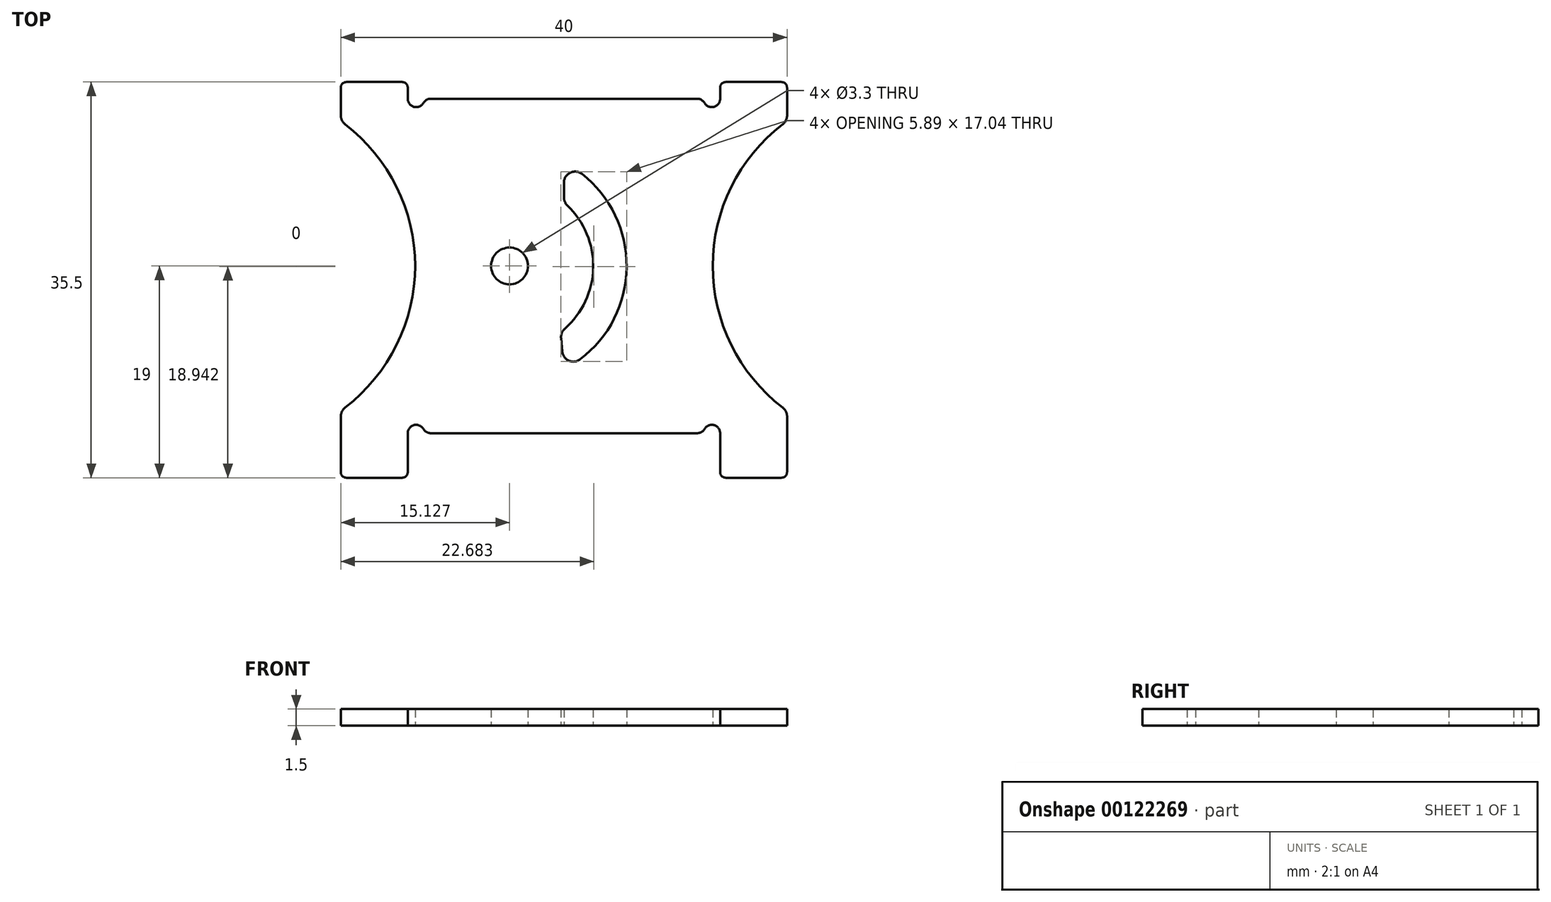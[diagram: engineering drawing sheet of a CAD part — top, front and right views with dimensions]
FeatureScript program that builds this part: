
annotation { "Feature Type Name" : "Feature", "Feature Type Description" : "" }
export const myFeature = defineFeature(function(context is Context, id is Id, definition is map)
    precondition{}
    {
        {
            var Q0;
            Q0=qCreatedBy(makeId("Top.planeOp"),FACE);
            var sketch = newSketch(context, id + "F0", { "sketchPlane" : qUnion([Q0])});
            skArc(sketch, "E0", {"start": v(19.6, 13.95) * mm, "mid": v(19.9, 14.3) * mm, "end": v(20, 14.74) * mm});
            skLineSegment(sketch, "E1", {"start": v(20, 14.74) * mm, "end": v(20, 17.25) * mm});
            skArc(sketch, "E2", {"start": v(20, 17.25) * mm, "mid": v(19.85, 17.6) * mm, "end": v(19.5, 17.75) * mm});
            skLineSegment(sketch, "E3", {"start": v(19.5, 17.75) * mm, "end": v(14.5, 17.75) * mm});
            skArc(sketch, "E4", {"start": v(14.5, 17.75) * mm, "mid": v(14.15, 17.6) * mm, "end": v(14, 17.25) * mm});
            skLineSegment(sketch, "E5", {"start": v(14, 17.25) * mm, "end": v(14, 16.25) * mm});
            skArc(sketch, "E6", {"start": v(12.6, 15.87) * mm, "mid": v(13.44, 15.53) * mm, "end": v(14, 16.25) * mm});
            skArc(sketch, "E7", {"start": v(12.6, 15.88) * mm, "mid": v(12.33, 16.15) * mm, "end": v(11.95, 16.25) * mm});
            skLineSegment(sketch, "E8", {"start": v(11.95, 16.25) * mm, "end": v(-11.95, 16.25) * mm});
            skArc(sketch, "E9", {"start": v(-11.95, 16.25) * mm, "mid": v(-12.33, 16.15) * mm, "end": v(-12.6, 15.88) * mm});
            skArc(sketch, "E10", {"start": v(-14, 16.25) * mm, "mid": v(-13.44, 15.53) * mm, "end": v(-12.6, 15.87) * mm});
            skLineSegment(sketch, "E11", {"start": v(-14, 16.25) * mm, "end": v(-14, 17.25) * mm});
            skArc(sketch, "E12", {"start": v(-14, 17.25) * mm, "mid": v(-14.15, 17.6) * mm, "end": v(-14.5, 17.75) * mm});
            skLineSegment(sketch, "E13", {"start": v(-14.5, 17.75) * mm, "end": v(-19.5, 17.75) * mm});
            skArc(sketch, "E14", {"start": v(-19.5, 17.75) * mm, "mid": v(-19.85, 17.6) * mm, "end": v(-20, 17.25) * mm});
            skLineSegment(sketch, "E15", {"start": v(-20, 17.25) * mm, "end": v(-20, 14.74) * mm});
            skArc(sketch, "E16", {"start": v(-20, 14.74) * mm, "mid": v(-19.9, 14.3) * mm, "end": v(-19.6, 13.95) * mm});
            skArc(sketch, "E17", {"start": v(-19.6, -11.45) * mm, "mid": v(-13.34, 1.25) * mm, "end": v(-19.6, 13.95) * mm});
            skArc(sketch, "E18", {"start": v(-19.6, -11.45) * mm, "mid": v(-19.9, -11.8) * mm, "end": v(-20, -12.24) * mm});
            skLineSegment(sketch, "E19", {"start": v(-20, -12.24) * mm, "end": v(-20, -17.25) * mm});
            skArc(sketch, "E20", {"start": v(-20, -17.25) * mm, "mid": v(-19.85, -17.6) * mm, "end": v(-19.5, -17.75) * mm});
            skLineSegment(sketch, "E21", {"start": v(-19.5, -17.75) * mm, "end": v(-14.5, -17.75) * mm});
            skArc(sketch, "E22", {"start": v(-14.5, -17.75) * mm, "mid": v(-14.15, -17.6) * mm, "end": v(-14, -17.25) * mm});
            skLineSegment(sketch, "E23", {"start": v(-14, -17.25) * mm, "end": v(-14, -13.75) * mm});
            skArc(sketch, "E24", {"start": v(-12.6, -13.37) * mm, "mid": v(-13.44, -13.03) * mm, "end": v(-14, -13.75) * mm});
            skArc(sketch, "E25", {"start": v(-12.6, -13.38) * mm, "mid": v(-12.33, -13.65) * mm, "end": v(-11.95, -13.75) * mm});
            skLineSegment(sketch, "E26", {"start": v(-11.95, -13.75) * mm, "end": v(11.95, -13.75) * mm});
            skArc(sketch, "E27", {"start": v(11.95, -13.75) * mm, "mid": v(12.33, -13.65) * mm, "end": v(12.6, -13.38) * mm});
            skArc(sketch, "E28", {"start": v(14, -13.75) * mm, "mid": v(13.44, -13.03) * mm, "end": v(12.6, -13.37) * mm});
            skLineSegment(sketch, "E29", {"start": v(14, -13.75) * mm, "end": v(14, -17.25) * mm});
            skArc(sketch, "E30", {"start": v(14, -17.25) * mm, "mid": v(14.15, -17.6) * mm, "end": v(14.5, -17.75) * mm});
            skLineSegment(sketch, "E31", {"start": v(14.5, -17.75) * mm, "end": v(19.5, -17.75) * mm});
            skArc(sketch, "E32", {"start": v(19.5, -17.75) * mm, "mid": v(19.85, -17.6) * mm, "end": v(20, -17.25) * mm});
            skLineSegment(sketch, "E33", {"start": v(20, -17.25) * mm, "end": v(20, -12.24) * mm});
            skArc(sketch, "E34", {"start": v(20, -12.24) * mm, "mid": v(19.9, -11.8) * mm, "end": v(19.6, -11.45) * mm});
            skArc(sketch, "E35", {"start": v(19.6, 13.95) * mm, "mid": v(13.34, 1.25) * mm, "end": v(19.6, -11.45) * mm});
            skLineSegment(sketch, "E36", {"start": v(2.63, 1.25) * mm, "end": v(-4.87, 1.25) * mm, "construction": true});
            skCircle(sketch, "E37", {"center": v(-4.87, 1.25) * mm, "radius": 1.65 * mm});
            skArc(sketch, "E38", {"start": v(2.63, 1.25) * mm, "mid": v(1.94, 4.39) * mm, "end": v(0, 6.95) * mm});
            skArc(sketch, "E39.MirrorCS", {"start": v(2.63, 1.25) * mm, "mid": v(1.85, -2.07) * mm, "end": v(-0.3, -4.7) * mm});
            skArc(sketch, "E40", {"start": v(5.63, 1.25) * mm, "mid": v(4.11, -4.19) * mm, "end": v(0, -8.05) * mm});
            skArc(sketch, "E41.MirrorCS", {"start": v(5.63, 1.25) * mm, "mid": v(4.11, 6.69) * mm, "end": v(0, 10.55) * mm});
            skLineSegment(sketch, "E42", {"start": v(0, 10.55) * mm, "end": v(0, 6.95) * mm});
            skLineSegment(sketch, "E43", {"start": v(0, -8.05) * mm, "end": v(-0.3, -4.7) * mm});
            skSolve(sketch);
        }
        {
            var Q0;
            Q0=qSketchRegion(id+"F0",true);
            extrude(context, id + "F1", {"entities" : qUnion([Q0]), "depth" : 1.5 * mm});
        }
        {
            var Q0;
            Q0=makeQuery(id+"F1.opExtrude","SWEPT_EDGE",EDGE,{"disambiguationData":[OSD([sQuery(id+"F0.wireOp",EDGE,"E41.MirrorCS"),sQuery(id+"F0.wireOp",EDGE,"E42")])]});
            var Q1;
            Q1=makeQuery(id+"F1.opExtrude","SWEPT_EDGE",EDGE,{"disambiguationData":[OSD([sQuery(id+"F0.wireOp",EDGE,"E39.MirrorCS"),sQuery(id+"F0.wireOp",EDGE,"E43")])]});
            var Q2;
            Q2=makeQuery(id+"F1.opExtrude","SWEPT_EDGE",EDGE,{"disambiguationData":[OSD([sQuery(id+"F0.wireOp",EDGE,"E40"),sQuery(id+"F0.wireOp",EDGE,"E43")])]});
            var Q3;
            Q3=makeQuery(id+"F1.opExtrude","SWEPT_EDGE",EDGE,{"disambiguationData":[OSD([sQuery(id+"F0.wireOp",EDGE,"E38"),sQuery(id+"F0.wireOp",EDGE,"E42")])]});
            fillet(context, id + "F2", {"entities" : qUnion([Q0, Q1, Q2, Q3]), "radius" : 1 * mm, "tangentPropagation" : true, "allowEdgeOverflow" : false});
        }
    });
